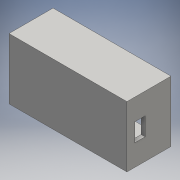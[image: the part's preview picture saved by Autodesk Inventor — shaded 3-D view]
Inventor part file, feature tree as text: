
AUTODESK INVENTOR PART (.ipt)
format: ipt  version: 2016 SP1 (Build 200210100, 210)  size: 165,376 bytes
history: native  units: mm
features: extrude x4, sketch x4, other x1
ambient origin geometry x8: Origin, YZ Plane, XZ Plane, XY Plane, X Axis, Y Axis, Z Axis, Center Point
bodies: Body1 (feature_tree)
feature tree (9):
  other  "Bryła1"
  extrude  "Wyciągnięcie proste1"  Depth=42.5mm
  extrude  "Wyciągnięcie proste2"  Depth=20.5mm
  extrude  "Wyciągnięcie proste3"  Depth=1.5mm
  extrude  "Wyciągnięcie proste4"  Depth=1.5mm
  sketch  "Szkic1"
  sketch  "Szkic2"
  sketch  "Szkic3"
  sketch  "Szkic4"
